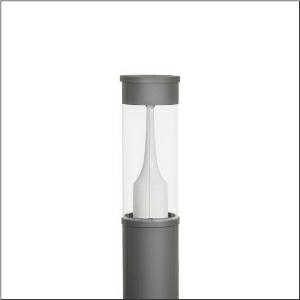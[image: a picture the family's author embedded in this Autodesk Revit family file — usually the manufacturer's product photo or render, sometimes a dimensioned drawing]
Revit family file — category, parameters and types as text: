
# Revit family: city-light_120_iq___pl1_2s_5xa5285rf14h_2286
name_source: partatom
category: Lighting Fixtures
units: mm (PartAtom-declared; Revit-internal decimal feet)

## family parameters
Cut with Voids When Loaded = No
Host = Face
Light Source = No
Part Type = Normal
Room Calculation Point = No
Round Connector Dimension = Use Diameter
Shared = No

## types (1)
- --- (1 x LED, 2970 lm, 18.5 W, 4000K)
    Apparent Load = 19 VA
    CIE Flux Codes = 23 62 94 96 100
    Color Rendering = 70
    Color Temperature = 4000K
    Default Elevation = 1800 mm
    Description = City-Light 120 iQ, bollard luminaire, Module 540 iQ-SR, primary light control with 3 zone facetted reflector, of plastic, silver coated, highly specular, structured, primary optical cover: cover, of PMMA, transparent, partly coated, light distribution: PL1.2s, primary light characteristic: symmetric, LED, High Power LED, rated luminous flux: 2.970lm, luminous efficacy: 161lm/W, light colour: 740, colour temperature: 4000K, control gear: iQ Street-Remote, control: pre-setting: logarithmic dimming characteristic, Street-Remote, Auto-Match, Temp-Guard, Lumen-Switch, Night-Set, Smart-Wire, Light-Fading, Desk-Remote (wireless, voltage-free reading and setting of iQ features in the workshop via application-optimized NFC function/RFID function), optimised constant luminous flux control (CLO 2.0), with terminal, 6-pole, max. 2.5mm², mains connection: 230..240V, AC, 50/60Hz, start of lifetime: 19W, end of service life: 20W, reduction: 9W, luminaire housing, cylindrical, of extruded aluminium section, coated, Siteco® metallic grey (DB 702S), length: 1.200mm, diameter: 200mm, Module 540 iQ-SR, traffic white (RAL 9016), equipment: standard, protection rating (complete): IP54, insulation class (complete): insulation class II (safety insulation), certification: CE, ENEC, VDE, packaging unit: 1 piece

Light Distribution: PL1.2s
    Height = 500 mm
    Lamp = 1 x LED
    Lamp Light Flux = 2970 lm
    Lamp Power = 18.5 W
    Lamp count = 1
    Length = 200 mm  [stored 0.656168 ft]
    Luminous efficacy = 161 lm/W
    Manufacturer = Siteco
    ModVariant = No
    Model = 5XA5285RF14H
    Mounting Place = Floor
    Mounting Type = Freestanding
    Number of Poles = 1
    OnlyDefault = Yes
    Power Factor = 1
    Product Name = City-Light 120 iQ | PL1.2s
    Product group = bollard luminaire
    ProductGroupID = 1304
    Protection Class = Protection class II
    Protection Degree = IP 54
    RLX_Detail_Level = 1
    RLX_Emergency_Light_Flux = 0 lm
    RLX_Emergency_Type = 0
    RLX_Emergency_Type_DB = No
    RlxData = <blob elided: 22385 chars, md5=4fa24029>
    Socket = socket
    Standby Power = 0 W
    System Light Flux = 2970 lm
    System Power = 19 W
    Type Comments = factory setting: luminous flux: 100 % | dim-lin: 254 | 385 mA
    Type Image = l_1006922.jpg
    URL = http://relux.com
    VarID = @adj_145158
    Voltage = 0 V
    Weight = 0.00 kg
    Width = 0 mm  [stored 0 ft]

note: [stored X ft] marks values corroborated as IEEE doubles in the binary element streams (Revit-internal decimal feet)

## geometry (parser evidence)
native form markers: Blend x4, Sweep x10
no freeform markers — native parametric forms only
